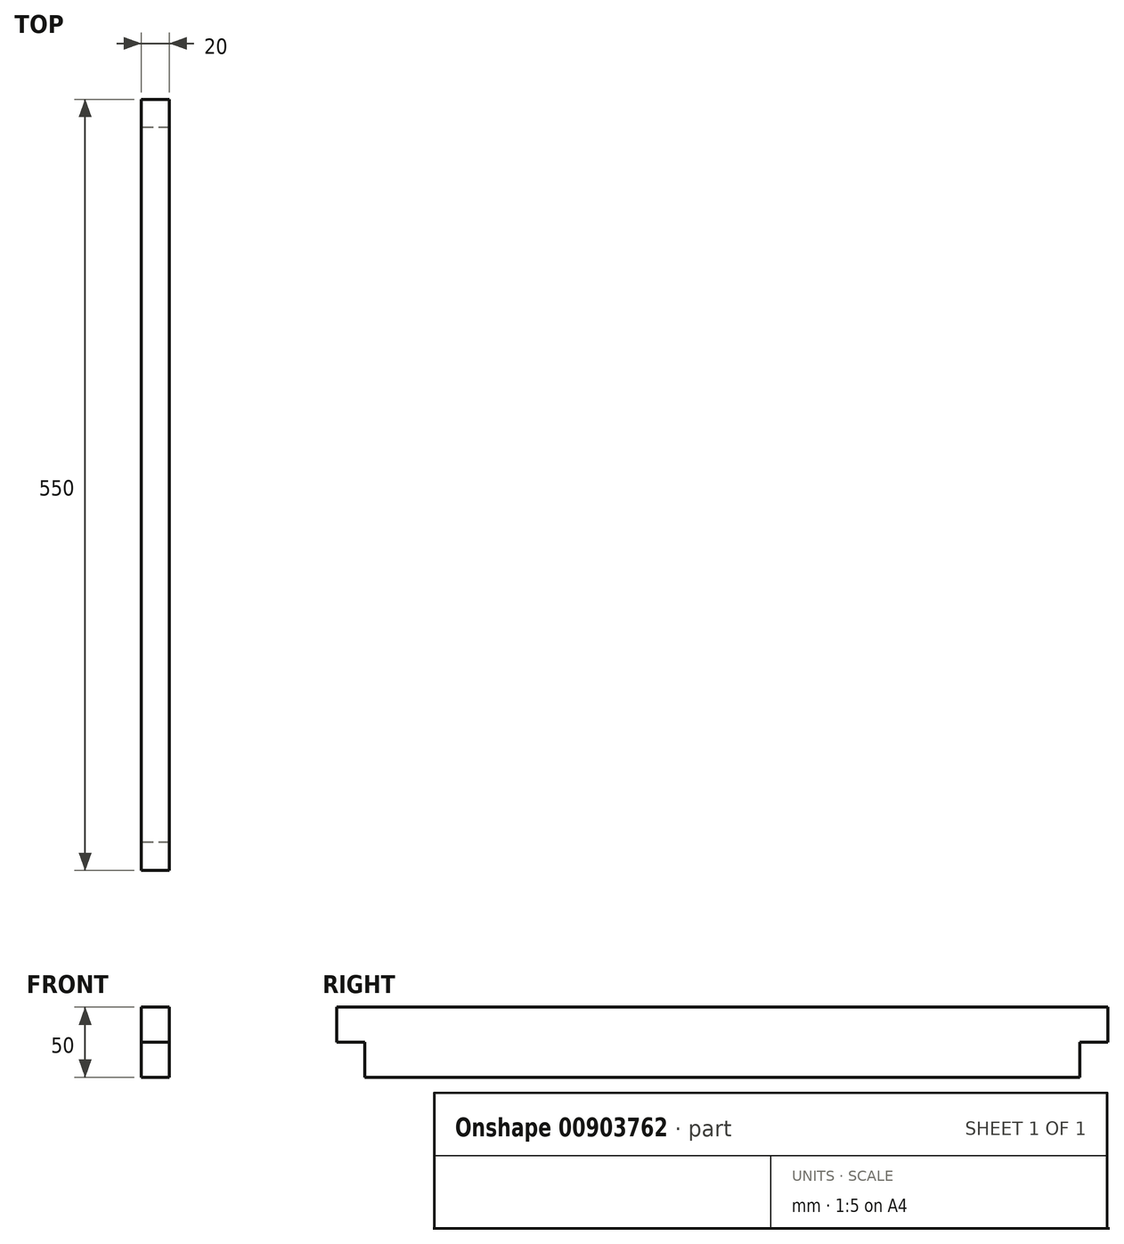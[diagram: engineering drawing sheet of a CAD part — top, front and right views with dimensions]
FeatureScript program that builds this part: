
annotation { "Feature Type Name" : "Feature", "Feature Type Description" : "" }
export const myFeature = defineFeature(function(context is Context, id is Id, definition is map)
    precondition{}
    {
        {
            var Q0;
            Q0=qCreatedBy(makeId("Right.planeOp"),FACE);
            var sketch = newSketch(context, id + "F0", { "sketchPlane" : qUnion([Q0])});
            skLineSegment(sketch, "E0.bottom", {"start": v(-275, 25) * mm, "end": v(275, 25) * mm});
            skLineSegment(sketch, "E0.top", {"start": v(-275, -25) * mm, "end": v(275, -25) * mm});
            skLineSegment(sketch, "E0.left", {"start": v(-275, 25) * mm, "end": v(-275, -25) * mm});
            skLineSegment(sketch, "E0.right", {"start": v(275, 25) * mm, "end": v(275, -25) * mm});
            skLineSegment(sketch, "E1", {"start": v(-275, 0) * mm, "end": v(-255, 0) * mm});
            skLineSegment(sketch, "E2", {"start": v(-255, 0) * mm, "end": v(-255, -25) * mm});
            skLineSegment(sketch, "E3.MirrorCS", {"start": v(275, 0) * mm, "end": v(255, 0) * mm});
            skLineSegment(sketch, "E4.MirrorCS", {"start": v(255, 0) * mm, "end": v(255, -25) * mm});
            skSolve(sketch);
        }
        {
            var Q0;
            {var subQ1=sQuery(id+"F0.wireOp",EDGE,"E0.bottom");Q0=makeQuery(id+"F0.imprint","IMPRINT",FACE,{"disambiguationData":[TD([[makeQuery(id+"F0.imprint","IMPRINT",EDGE,{"derivedFrom":subQ1}),-1.0]])]});}
            extrude(context, id + "F1", {"entities" : qUnion([Q0]), "depth" : 20 * mm, "offsetDistance" : 25 * mm});
        }
    });
